# Revit family: Gira_2003100
name_source: partatom
category: Electrical Fixtures
revit_build: Autodesk Revit 2017 (Build: 20160225_1515(x64)
units: mm (PartAtom-declared; Revit-internal decimal feet)

## family parameters
Cut with Voids When Loaded = No
Host = Face
Maintain Annotation Orientation = Yes
Part Type = Normal
Room Calculation Point = No
Round Connector Dimension = Use Diameter
Shared = No

## types (1)
- Tastsens.2 3f 24 V pot.frei BSF System 55 Klar/Reinweiß
    Andere Bussysteme = ohne
    Anzahl der Betätigungspunkte = 6
    Anzahl der Tasten = 3
    Ausführung der Oberfläche = glänzend
    Available = Yes
    Bussystem Funkbus = Yes
    Bussystem KNX = Yes
    Bussystem KNX-Funk = No
    Bussystem LON = No
    Bussystem Powernet = No
    Category = Bussystem-Tastsensor
    Data sheet (1) = https://katalog.gira.de
    Default Elevation = 1219 mm
    Farbe = weiß
    GTIN = 4010337047971
    HAN = 2003100
    HeinzeBIM = https://bimportal.heinze.de
    Manufacturer URL = https://www.gira.de
    Mit Beschriftungsfeld = Yes
    Mit Busankopplung = No
    Mit Diebstahl-/Demontageschutz = No
    Mit Display = No
    Mit Infrarotsensor = No
    Mit LED-Anzeige = Yes
    Mit Raumthermostat = No
    Model = Sys55_Komplettgerät_Schalten und Tasten
    Montageart = unter Putz
    Name = Tastsens.2 3f 24 V pot.frei BSF System 55 Klar/Reinweiß
    Oberfläche = sonstige
    Region = DE
    Schutzart (IP) = IP20
    Transparent = Yes
    URL = http://katalog.gira.de
    Werkstoff = sonstige
    Werkstoffgüte = sonstige

## geometry (parser evidence)
native form markers: Blend x2, Sweep x8
no freeform markers — native parametric forms only
